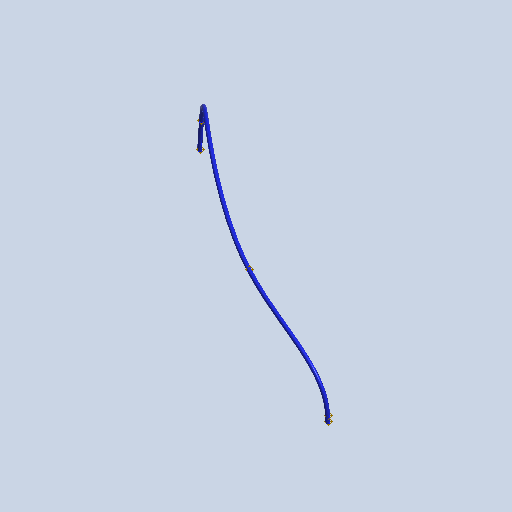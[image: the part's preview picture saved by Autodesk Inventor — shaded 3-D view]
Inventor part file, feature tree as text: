
AUTODESK INVENTOR PART (.ipt)
format: ipt  version: 2023.1 (Build 271208000, 208)  size: 111,104 bytes
history: native  units: mm (DEFAULTED — no unit token found)
features: other x7, plane x1, sketch x1, sweep x1
ambient origin geometry x8: Origin, YZ Plane, XZ Plane, XY Plane, X Axis, Y Axis, Z Axis, Center Point
bodies: Body1 (feature_tree)
feature tree (10):
  other  "Work Point1"
  other  "Work Point2"
  other  "Segment1"
  plane  "Work Plane1"
  other  "Work Point3"
  other  "Work Point4"
  other  "Work Point5"
  sketch  "Sketch1"  dims[d0=0.0mm d1=0.0mm]
  other  "Srf1"
  sweep  "SweepSrf1"
